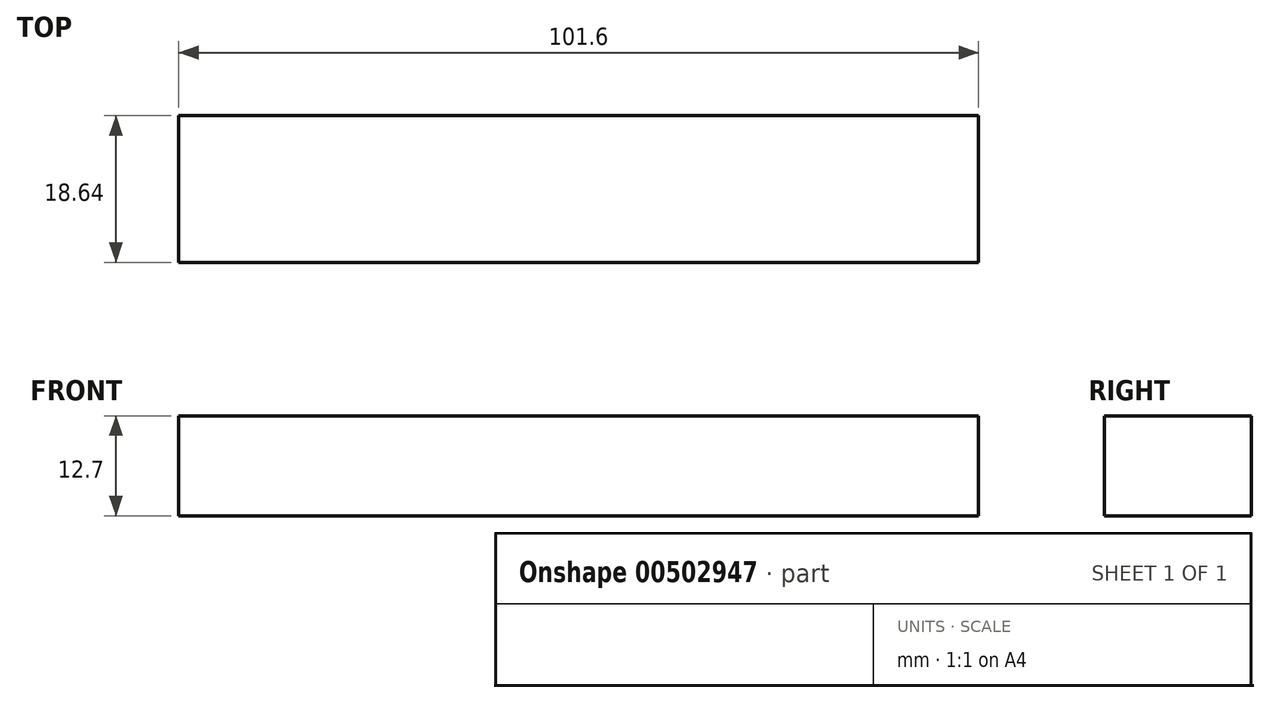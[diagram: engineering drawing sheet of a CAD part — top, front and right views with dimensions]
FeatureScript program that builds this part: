
annotation { "Feature Type Name" : "Feature", "Feature Type Description" : "" }
export const myFeature = defineFeature(function(context is Context, id is Id, definition is map)
    precondition{}
    {
        {
            var Q0;
            Q0=qCreatedBy(makeId("Top.planeOp"),FACE);
            var sketch = newSketch(context, id + "F0", { "sketchPlane" : qUnion([Q0])});
            skLineSegment(sketch, "E0.bottom", {"start": v(50.8, -9.32) * mm, "end": v(-50.8, -9.32) * mm});
            skLineSegment(sketch, "E0.top", {"start": v(50.8, 9.32) * mm, "end": v(-50.8, 9.32) * mm});
            skLineSegment(sketch, "E0.left", {"start": v(50.8, -9.32) * mm, "end": v(50.8, 9.32) * mm});
            skLineSegment(sketch, "E0.right", {"start": v(-50.8, -9.32) * mm, "end": v(-50.8, 9.32) * mm});
            skPoint(sketch, "E0.middle", {"position": v(0, 0) * mm});
            skSolve(sketch);
        }
        {
            var Q0;
            Q0 = qSketchRegion(id + "F0", true);
            extrude(context, id + "F1", {"entities" : qUnion([Q0]), "depth" : 12.7 * mm, "offsetDistance" : 25.4 * mm});
        }
    });
